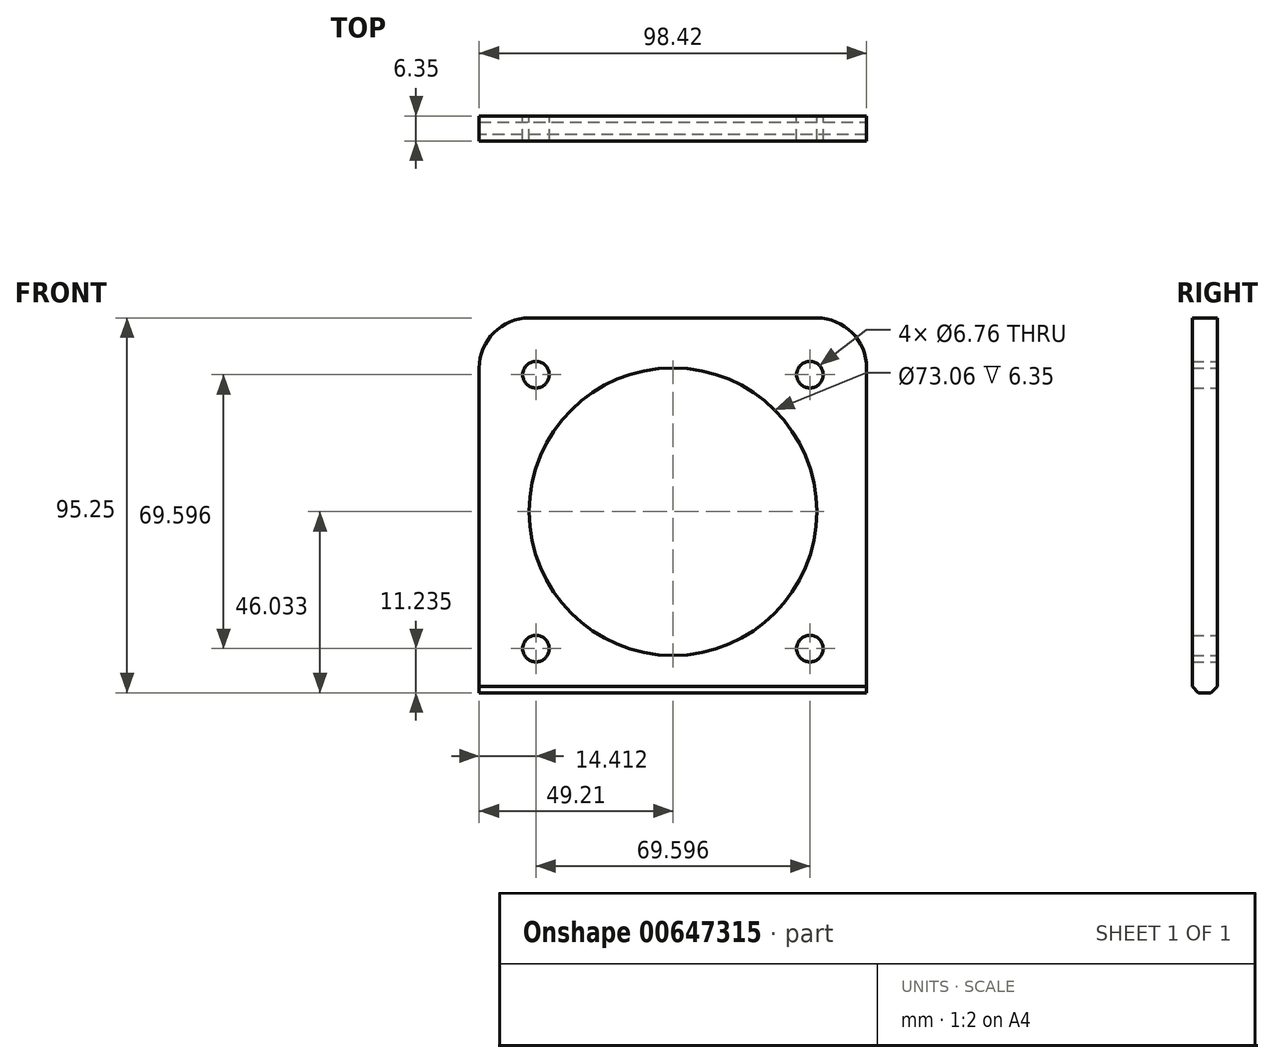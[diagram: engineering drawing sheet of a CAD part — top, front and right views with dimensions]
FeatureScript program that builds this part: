
annotation { "Feature Type Name" : "Feature", "Feature Type Description" : "" }
export const myFeature = defineFeature(function(context is Context, id is Id, definition is map)
    precondition{}
    {
        {
            var Q0;
            Q0=qCreatedBy(makeId("Front.planeOp"),FACE);
            var sketch = newSketch(context, id + "F0", { "sketchPlane" : qUnion([Q0])});
            skLineSegment(sketch, "E0", {"start": v(-169.18, 87.18) * mm, "end": v(-248.16, 87.18) * mm});
            skLineSegment(sketch, "E1", {"start": v(-248.16, 87.18) * mm, "end": v(-248.9, 87.1) * mm});
            skLineSegment(sketch, "E2", {"start": v(-248.9, 87.1) * mm, "end": v(-249.59, 86.85) * mm});
            skLineSegment(sketch, "E3", {"start": v(-249.59, 86.85) * mm, "end": v(-250.24, 86.45) * mm});
            skLineSegment(sketch, "E4", {"start": v(-250.24, 86.45) * mm, "end": v(-250.99, 85.91) * mm});
            skLineSegment(sketch, "E5", {"start": v(-250.99, 85.91) * mm, "end": v(-251.4, 85.3) * mm});
            skLineSegment(sketch, "E6", {"start": v(-251.4, 85.3) * mm, "end": v(-251.64, 84.6) * mm});
            skLineSegment(sketch, "E7", {"start": v(-251.64, 84.6) * mm, "end": v(-251.72, 83.87) * mm});
            skLineSegment(sketch, "E8", {"start": v(-251.72, 83.87) * mm, "end": v(-251.72, 4.86) * mm});
            skLineSegment(sketch, "E9", {"start": v(-251.72, 4.86) * mm, "end": v(-251.64, 4.12) * mm});
            skLineSegment(sketch, "E10", {"start": v(-251.64, 4.12) * mm, "end": v(-251.4, 3.43) * mm});
            skLineSegment(sketch, "E11", {"start": v(-251.4, 3.43) * mm, "end": v(-250.99, 2.81) * mm});
            skLineSegment(sketch, "E12", {"start": v(-250.99, 2.81) * mm, "end": v(-250.24, 2.28) * mm});
            skLineSegment(sketch, "E13", {"start": v(-250.24, 2.28) * mm, "end": v(-249.59, 1.91) * mm});
            skLineSegment(sketch, "E14", {"start": v(-249.59, 1.91) * mm, "end": v(-248.9, 1.67) * mm});
            skLineSegment(sketch, "E15", {"start": v(-248.9, 1.67) * mm, "end": v(-248.16, 1.58) * mm});
            skLineSegment(sketch, "E16", {"start": v(-248.16, 1.58) * mm, "end": v(-169.18, 1.58) * mm});
            skLineSegment(sketch, "E17", {"start": v(-169.18, 1.58) * mm, "end": v(-168.45, 1.67) * mm});
            skLineSegment(sketch, "E18", {"start": v(-168.45, 1.67) * mm, "end": v(-167.75, 1.91) * mm});
            skLineSegment(sketch, "E19", {"start": v(-167.75, 1.91) * mm, "end": v(-167.1, 2.28) * mm});
            skLineSegment(sketch, "E20", {"start": v(-167.1, 2.28) * mm, "end": v(-166.6, 2.81) * mm});
            skLineSegment(sketch, "E21", {"start": v(-166.6, 2.81) * mm, "end": v(-165.94, 3.43) * mm});
            skLineSegment(sketch, "E22", {"start": v(-165.94, 3.43) * mm, "end": v(-165.7, 4.12) * mm});
            skLineSegment(sketch, "E23", {"start": v(-165.7, 4.12) * mm, "end": v(-165.62, 4.86) * mm});
            skLineSegment(sketch, "E24", {"start": v(-165.62, 4.86) * mm, "end": v(-165.62, 83.87) * mm});
            skLineSegment(sketch, "E25", {"start": v(-165.62, 83.87) * mm, "end": v(-165.7, 84.6) * mm});
            skLineSegment(sketch, "E26", {"start": v(-165.7, 84.6) * mm, "end": v(-165.94, 85.3) * mm});
            skLineSegment(sketch, "E27", {"start": v(-165.94, 85.3) * mm, "end": v(-166.6, 85.91) * mm});
            skLineSegment(sketch, "E28", {"start": v(-166.6, 85.91) * mm, "end": v(-167.1, 86.45) * mm});
            skLineSegment(sketch, "E29", {"start": v(-167.1, 86.45) * mm, "end": v(-167.75, 86.85) * mm});
            skLineSegment(sketch, "E30", {"start": v(-167.75, 86.85) * mm, "end": v(-168.45, 87.1) * mm});
            skLineSegment(sketch, "E31", {"start": v(-168.45, 87.1) * mm, "end": v(-169.18, 87.18) * mm});
            skCircle(sketch, "E32", {"center": v(-208.7, 44.36) * mm, "radius": 36.52 * mm});
            skArc(sketch, "E33", {"start": v(-213.15, 48.86) * mm, "mid": v(-212.82, 39.56) * mm, "end": v(-203.58, 40.62) * mm});
            skArc(sketch, "E34", {"start": v(-203.58, 48.1) * mm, "mid": v(-203.89, 48.5) * mm, "end": v(-204.23, 48.86) * mm});
            skCircle(sketch, "E35", {"center": v(-208.7, 44.36) * mm, "radius": 6.91 * mm});
            skCircle(sketch, "E36", {"center": v(-208.7, 44.36) * mm, "radius": 9.15 * mm});
            skLineSegment(sketch, "E37", {"start": v(-213.15, 48.86) * mm, "end": v(-204.23, 48.86) * mm});
            skLineSegment(sketch, "E38", {"start": v(-203.58, 40.62) * mm, "end": v(-203.58, 48.1) * mm});
            skSolve(sketch);
        }
        {
            var Q0;
            Q0=makeQuery(id+"F0.imprint","IMPRINT",FACE,{"disambiguationData":[TD([[makeQuery(id+"F0.imprint","IMPRINT",EDGE,{"derivedFrom":sQuery(id+"F0.wireOp",EDGE,"E0")}),1.0]])]});
            var sketch = newSketch(context, id + "F1", { "sketchPlane" : qUnion([Q0])});
            skLineSegment(sketch, "E39", {"start": v(-159.48, 93.58) * mm, "end": v(-159.48, -1.67) * mm});
            skLineSegment(sketch, "E40", {"start": v(-257.9, 93.58) * mm, "end": v(-257.9, -1.67) * mm});
            skLineSegment(sketch, "E41", {"start": v(-257.9, 93.58) * mm, "end": v(-159.48, 93.58) * mm});
            skLineSegment(sketch, "E42", {"start": v(-159.48, -1.67) * mm, "end": v(-257.9, -1.67) * mm});
            skPoint(sketch, "E43.0", {"position": v(-173.9, 79.16) * mm});
            skPoint(sketch, "E44.0", {"position": v(-243.49, 79.16) * mm});
            skPoint(sketch, "E45.0", {"position": v(-243.49, 9.56) * mm});
            skPoint(sketch, "E46.0", {"position": v(-173.9, 9.56) * mm});
            skPoint(sketch, "E47.0", {"position": v(-208.7, 44.36) * mm});
            skCircle(sketch, "E48", {"center": v(-208.7, 44.36) * mm, "radius": 36.53 * mm});
            skSolve(sketch);
        }
        {
            var Q0;
            Q0=makeQuery(id+"F1.imprint","IMPRINT",FACE,{"disambiguationData":[TD([[makeQuery(id+"F1.imprint","IMPRINT",EDGE,{"derivedFrom":sQuery(id+"F1.wireOp",EDGE,"E39")}),-1.0]])]});
            var Q1;
            Q1=makeQuery(id+"F1.imprint","IMPRINT",FACE,{"disambiguationData":[TD([[makeQuery(id+"F1.imprint","IMPRINT",EDGE,{"derivedFrom":sQuery(id+"F1.wireOp",EDGE,"E48")}),-1.0]])]});
            var Q2;
            Q2=makeQuery(id+"F1.imprint","IMPRINT",FACE,{"disambiguationData":[TD([[makeQuery(id+"F1.imprint","IMPRINT",EDGE,{"derivedFrom":makeQuery(id+"F0.imprint","IMPRINT",EDGE,{"derivedFrom":sQuery(id+"F0.wireOp",EDGE,"522af4eb-6f52-476e-a678-d99e9d9153fa")})}),-1.0]])]});
            var Q3;
            Q3=makeQuery(id+"F1.imprint","IMPRINT",FACE,{"disambiguationData":[TD([[makeQuery(id+"F1.imprint","IMPRINT",EDGE,{"derivedFrom":makeQuery(id+"F0.imprint","IMPRINT",EDGE,{"derivedFrom":sQuery(id+"F0.wireOp",EDGE,"8c842abd-af80-4940-82d1-f0c0380c5157")})}),-1.0]])]});
            var Q4;
            Q4=makeQuery(id+"F1.imprint","IMPRINT",FACE,{"disambiguationData":[TD([[makeQuery(id+"F1.imprint","IMPRINT",EDGE,{"derivedFrom":makeQuery(id+"F0.imprint","IMPRINT",EDGE,{"derivedFrom":sQuery(id+"F0.wireOp",EDGE,"1bba6191-04dd-48ec-ad11-057d2432ccd8")})}),-1.0]])]});
            var Q5;
            Q5=makeQuery(id+"F1.imprint","IMPRINT",FACE,{"disambiguationData":[TD([[makeQuery(id+"F1.imprint","IMPRINT",EDGE,{"derivedFrom":makeQuery(id+"F0.imprint","IMPRINT",EDGE,{"derivedFrom":sQuery(id+"F0.wireOp",EDGE,"a90dd077-cdd2-4f4e-b432-149809708848")})}),-1.0]])]});
            extrude(context, id + "F2", {"entities" : qUnion([Q0, Q1, Q2, Q3, Q4, Q5]), "depth" : 6.35 * mm, "offsetDistance" : 25.4 * mm});
        }
        {
            var Q0;
            Q0=makeQuery(id+"F2.opExtrude","SWEPT_EDGE",EDGE,{"disambiguationData":[OSD([sQuery(id+"F1.wireOp",EDGE,"E40"),sQuery(id+"F1.wireOp",EDGE,"E41")])]});
            var Q1;
            Q1=makeQuery(id+"F2.opExtrude","SWEPT_EDGE",EDGE,{"disambiguationData":[OSD([sQuery(id+"F1.wireOp",EDGE,"E39"),sQuery(id+"F1.wireOp",EDGE,"E41")])]});
            fillet(context, id + "F3", {"entities" : qUnion([Q0, Q1]), "radius" : 12.7 * mm, "tangentPropagation" : true, "allowEdgeOverflow" : false});
        }
        {
            var Q0;
            Q0=makeQuery(id+"F2.opExtrude","CAP_EDGE",EDGE,{"disambiguationData":[OSD([sQuery(id+"F1.wireOp",EDGE,"E42")])],"isStart":true});
            var Q1;
            Q1=makeQuery(id+"F2.opExtrude","CAP_EDGE",EDGE,{"disambiguationData":[OSD([sQuery(id+"F1.wireOp",EDGE,"E42")])],"isStart":false});
            chamfer(context, id + "F4", {"entities" : qUnion([Q0, Q1]), "width" : 1.59 * mm, "tangentPropagation" : true});
        }
        {
            var Q0;
            Q0=sQuery(id+"F1.wireOp",VERTEX,"E44.0");
            var Q1;
            Q1=sQuery(id+"F1.wireOp",VERTEX,"E43.0");
            var Q2;
            Q2=sQuery(id+"F1.wireOp",VERTEX,"E46.0");
            var Q3;
            Q3=sQuery(id+"F1.wireOp",VERTEX,"E45.0");
            var Q4;
            Q4=makeQuery(id+"F2.opExtrude","SWEPT_BODY",BODY,{"disambiguationData":[OSD([sQuery(id+"F1.wireOp",EDGE,"E39"),sQuery(id+"F1.wireOp",EDGE,"E40"),sQuery(id+"F1.wireOp",EDGE,"E41"),sQuery(id+"F1.wireOp",EDGE,"E42"),sQuery(id+"F1.wireOp",EDGE,"Pvu4lvdr-CNw6-Qwbr-gy02-vZhBIzCig3s9"),sQuery(id+"F1.wireOp",EDGE,"d0583d14-0689-4c07-9302-67f06a6a9e60"),sQuery(id+"F1.wireOp",EDGE,"2774e060-0362-42a0-984e-d2fe1e74eac9"),sQuery(id+"F1.wireOp",EDGE,"6baa20f6-fc59-4b95-a89d-e32fc1ab5bc1"),sQuery(id+"F1.wireOp",EDGE,"E48")])]});
            hole(context, id + "F5", {"style" : HoleStyle.SIMPLE, "endStyle" : HoleEndStyle.THROUGH, "oppositeDirection" : true, "standardTappedOrClearance" : lookupTablePath({ "standard" : "ANSI", "fit" : "Normal (ASME)", "size" : "1/4", "type" : "Clearance" }), "standardBlindInLast" : lookupTablePath({ "fit" : "Free", "standard" : "ANSI", "size" : "1/4", "type" : "Clearance" }), "holeDiameter" : 6.76 * mm, "majorDiameter" : 6.35 * mm, "isTappedThrough" : true, "tappedDepth" : 12.7 * mm, "tapClearance" : 3, "startFromSketch" : true, "locations" : qUnion([Q0, Q1, Q2, Q3]), "scope" : qUnion([Q4])});
        }
    });
